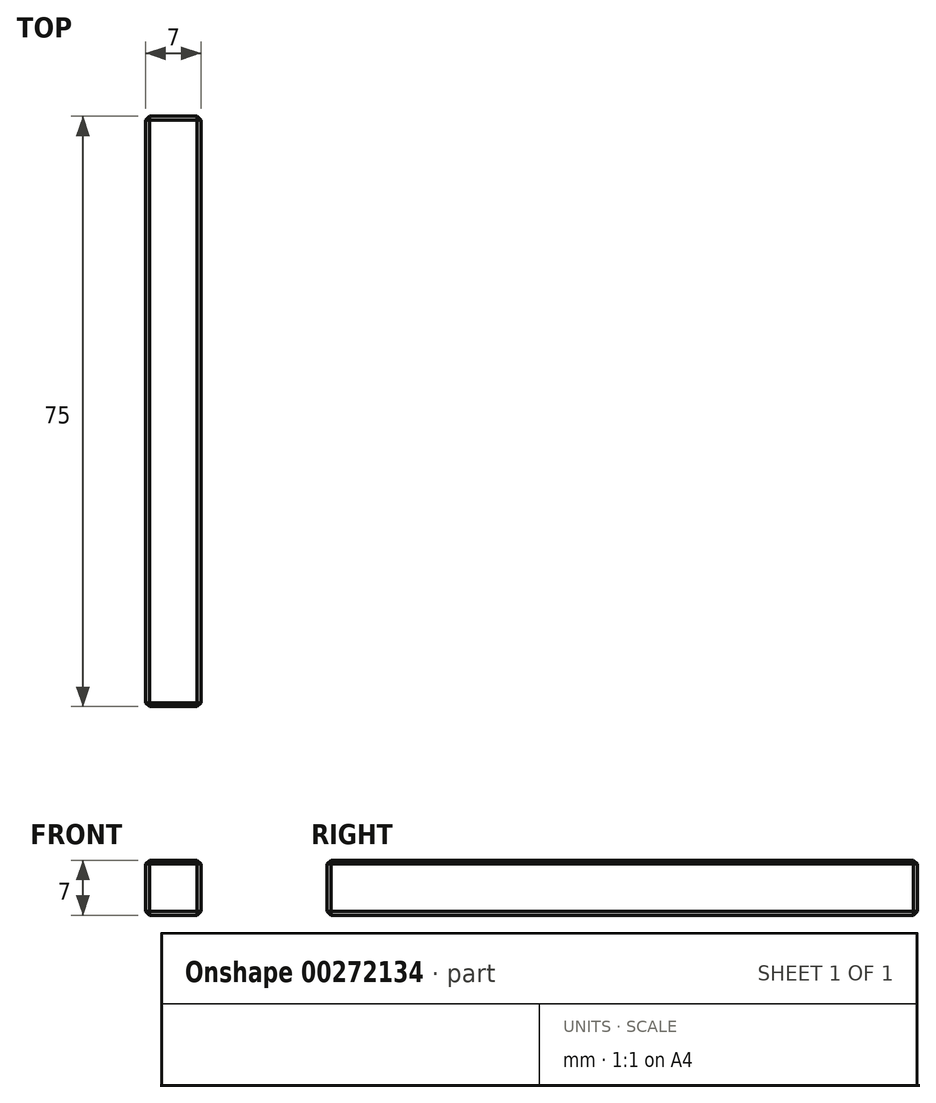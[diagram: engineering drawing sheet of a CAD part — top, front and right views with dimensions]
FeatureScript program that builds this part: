
annotation { "Feature Type Name" : "Feature", "Feature Type Description" : "" }
export const myFeature = defineFeature(function(context is Context, id is Id, definition is map)
    precondition{}
    {
        {
            var Q0;
            Q0=qCreatedBy(makeId("Front.planeOp"),FACE);
            var sketch = newSketch(context, id + "F0", { "sketchPlane" : qUnion([Q0])});
            skLineSegment(sketch, "E0.bottom", {"start": v(3.5, -3.5) * mm, "end": v(-3.5, -3.5) * mm});
            skLineSegment(sketch, "E0.top", {"start": v(3.5, 3.5) * mm, "end": v(-3.5, 3.5) * mm});
            skLineSegment(sketch, "E0.left", {"start": v(3.5, -3.5) * mm, "end": v(3.5, 3.5) * mm});
            skLineSegment(sketch, "E0.right", {"start": v(-3.5, -3.5) * mm, "end": v(-3.5, 3.5) * mm});
            skPoint(sketch, "E0.middle", {"position": v(0, 0) * mm});
            skSolve(sketch);
        }
        {
            var Q0;
            Q0=makeQuery(id+"F0.imprint","IMPRINT",FACE,{"disambiguationData":[TD([[makeQuery(id+"F0.imprint","IMPRINT",EDGE,{"derivedFrom":sQuery(id+"F0.wireOp",EDGE,"E0.bottom")}),-1.0]])]});
            extrude(context, id + "F1", {"entities" : qUnion([Q0]), "endBound" : BoundingType.SYMMETRIC, "depth" : 75 * mm});
        }
        {
            var Q0;
            Q0=makeQuery(id+"F1.opExtrude","CAP_FACE",FACE,{"disambiguationData":[OSD([sQuery(id+"F0.wireOp",EDGE,"E0.bottom"),sQuery(id+"F0.wireOp",EDGE,"E0.top"),sQuery(id+"F0.wireOp",EDGE,"E0.left"),sQuery(id+"F0.wireOp",EDGE,"E0.right")])],"isStart":false});
            var Q1;
            Q1=makeQuery(id+"F1.opExtrude","SWEPT_EDGE",EDGE,{"disambiguationData":[OSD([sQuery(id+"F0.wireOp",EDGE,"E0.top"),sQuery(id+"F0.wireOp",EDGE,"E0.left")])]});
            var Q2;
            Q2=makeQuery(id+"F1.opExtrude","SWEPT_EDGE",EDGE,{"disambiguationData":[OSD([sQuery(id+"F0.wireOp",EDGE,"E0.bottom"),sQuery(id+"F0.wireOp",EDGE,"E0.left")])]});
            var Q3;
            Q3=makeQuery(id+"F1.opExtrude","SWEPT_EDGE",EDGE,{"disambiguationData":[OSD([sQuery(id+"F0.wireOp",EDGE,"E0.top"),sQuery(id+"F0.wireOp",EDGE,"E0.right")])]});
            var Q4;
            Q4=makeQuery(id+"F1.opExtrude","SWEPT_EDGE",EDGE,{"disambiguationData":[OSD([sQuery(id+"F0.wireOp",EDGE,"E0.bottom"),sQuery(id+"F0.wireOp",EDGE,"E0.right")])]});
            var Q5;
            Q5=makeQuery(id+"F1.opExtrude","CAP_FACE",FACE,{"disambiguationData":[OSD([sQuery(id+"F0.wireOp",EDGE,"E0.bottom"),sQuery(id+"F0.wireOp",EDGE,"E0.top"),sQuery(id+"F0.wireOp",EDGE,"E0.left"),sQuery(id+"F0.wireOp",EDGE,"E0.right")])],"isStart":true});
            chamfer(context, id + "F2", {"entities" : qUnion([Q0, Q1, Q2, Q3, Q4, Q5]), "width" : 0.5 * mm, "tangentPropagation" : true});
        }
    });
